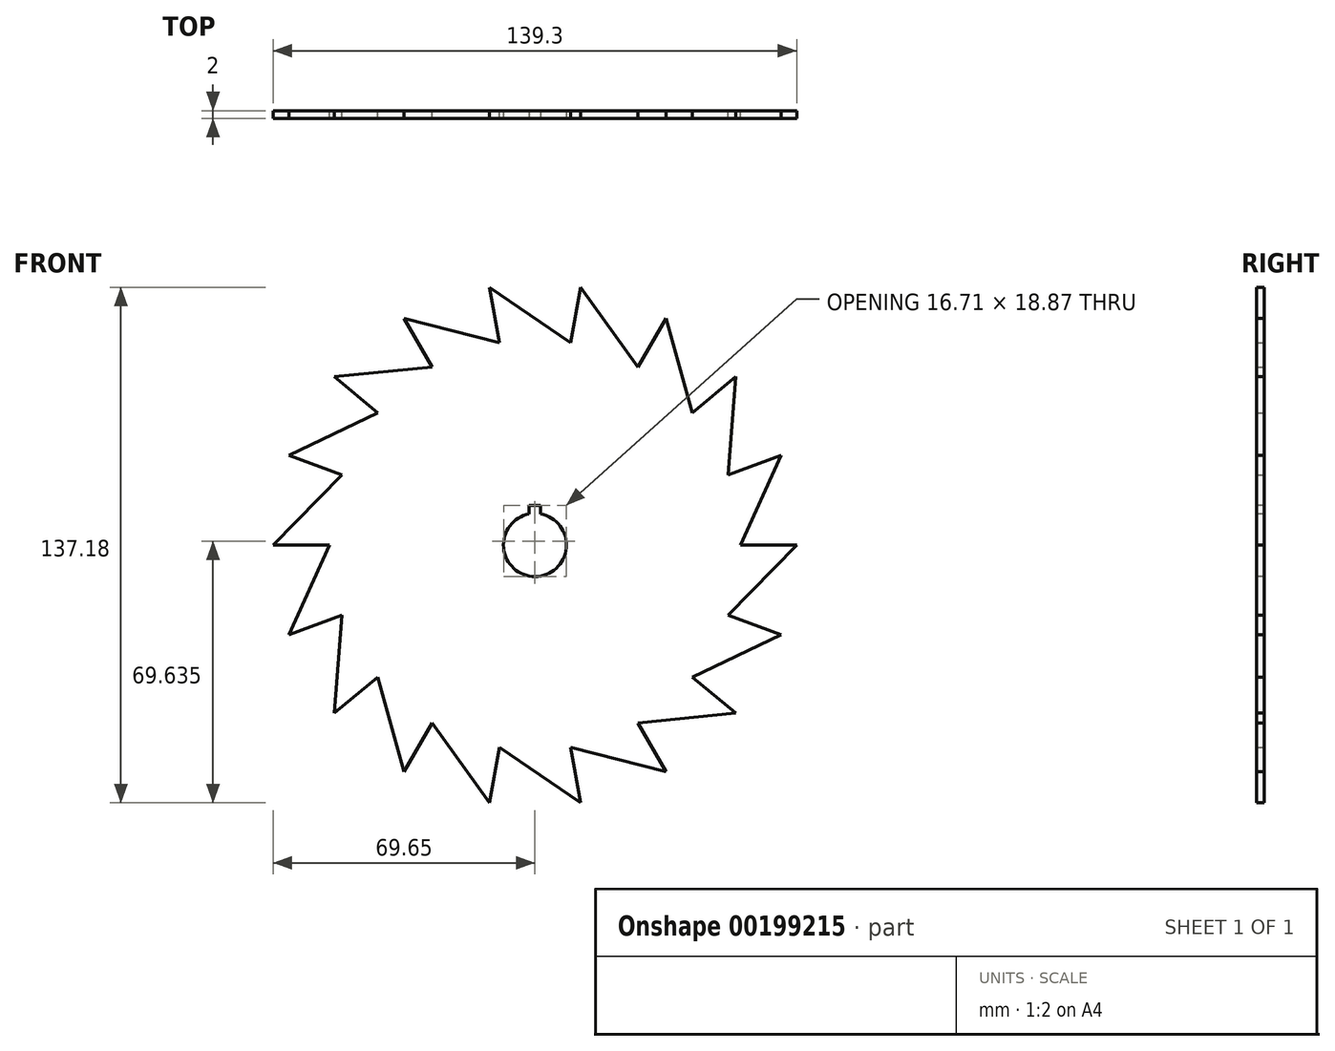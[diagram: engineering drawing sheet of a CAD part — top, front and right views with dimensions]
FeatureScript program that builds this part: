
annotation { "Feature Type Name" : "Feature", "Feature Type Description" : "" }
export const myFeature = defineFeature(function(context is Context, id is Id, definition is map)
    precondition{}
    {
        {
            var Q0;
            Q0=qCreatedBy(makeId("Front.planeOp"),FACE);
            var sketch = newSketch(context, id + "F0", { "sketchPlane" : qUnion([Q0])});
            skCircle(sketch, "E0", {"center": v(0, 0) * mm, "radius": 54.65 * mm, "construction": true});
            skCircle(sketch, "E1.0", {"center": v(0, 0) * mm, "radius": 69.65 * mm, "construction": true});
            skLineSegment(sketch, "E2", {"start": v(0, 0) * mm, "end": v(51.35, 18.7) * mm, "construction": true});
            skLineSegment(sketch, "E3", {"start": v(65.45, 23.82) * mm, "end": v(54.65, 0) * mm});
            skLineSegment(sketch, "E4", {"start": v(51.35, 18.7) * mm, "end": v(65.45, 23.82) * mm});
            skLineSegment(sketch, "E5.1.0", {"start": v(53.35, 44.77) * mm, "end": v(51.35, 18.7) * mm});
            skLineSegment(sketch, "E5.1.1", {"start": v(41.86, 35.13) * mm, "end": v(53.35, 44.77) * mm});
            skLineSegment(sketch, "E5.2.0", {"start": v(34.82, 60.32) * mm, "end": v(41.86, 35.13) * mm});
            skLineSegment(sketch, "E5.2.1", {"start": v(27.32, 47.33) * mm, "end": v(34.82, 60.32) * mm});
            skLineSegment(sketch, "E5.3.0", {"start": v(12.1, 68.6) * mm, "end": v(27.32, 47.33) * mm});
            skLineSegment(sketch, "E5.3.1", {"start": v(9.49, 53.82) * mm, "end": v(12.1, 68.6) * mm});
            skLineSegment(sketch, "E5.4.0", {"start": v(-12.1, 68.6) * mm, "end": v(9.49, 53.82) * mm});
            skLineSegment(sketch, "E5.4.1", {"start": v(-9.49, 53.82) * mm, "end": v(-12.1, 68.6) * mm});
            skLineSegment(sketch, "E5.5.0", {"start": v(-34.82, 60.32) * mm, "end": v(-9.49, 53.82) * mm});
            skLineSegment(sketch, "E5.5.1", {"start": v(-27.32, 47.33) * mm, "end": v(-34.82, 60.32) * mm});
            skLineSegment(sketch, "E5.6.0", {"start": v(-53.35, 44.77) * mm, "end": v(-27.32, 47.33) * mm});
            skLineSegment(sketch, "E5.6.1", {"start": v(-41.86, 35.13) * mm, "end": v(-53.35, 44.77) * mm});
            skLineSegment(sketch, "E5.7.0", {"start": v(-65.45, 23.82) * mm, "end": v(-41.86, 35.13) * mm});
            skLineSegment(sketch, "E5.7.1", {"start": v(-51.35, 18.7) * mm, "end": v(-65.45, 23.82) * mm});
            skLineSegment(sketch, "E5.8.0", {"start": v(-69.65, 0) * mm, "end": v(-51.35, 18.7) * mm});
            skLineSegment(sketch, "E5.8.1", {"start": v(-54.65, 0) * mm, "end": v(-69.65, 0) * mm});
            skLineSegment(sketch, "E5.9.0", {"start": v(-65.45, -23.82) * mm, "end": v(-54.65, 0) * mm});
            skLineSegment(sketch, "E5.9.1", {"start": v(-51.35, -18.7) * mm, "end": v(-65.45, -23.82) * mm});
            skLineSegment(sketch, "E5.10.0", {"start": v(-53.35, -44.77) * mm, "end": v(-51.35, -18.7) * mm});
            skLineSegment(sketch, "E5.10.1", {"start": v(-41.86, -35.13) * mm, "end": v(-53.35, -44.77) * mm});
            skLineSegment(sketch, "E5.11.0", {"start": v(-34.82, -60.32) * mm, "end": v(-41.86, -35.13) * mm});
            skLineSegment(sketch, "E5.11.1", {"start": v(-27.32, -47.33) * mm, "end": v(-34.82, -60.32) * mm});
            skLineSegment(sketch, "E5.12.0", {"start": v(-12.1, -68.6) * mm, "end": v(-27.32, -47.33) * mm});
            skLineSegment(sketch, "E5.12.1", {"start": v(-9.49, -53.82) * mm, "end": v(-12.1, -68.6) * mm});
            skLineSegment(sketch, "E5.13.0", {"start": v(12.1, -68.6) * mm, "end": v(-9.49, -53.82) * mm});
            skLineSegment(sketch, "E5.13.1", {"start": v(9.49, -53.82) * mm, "end": v(12.1, -68.6) * mm});
            skLineSegment(sketch, "E5.14.0", {"start": v(34.82, -60.32) * mm, "end": v(9.49, -53.82) * mm});
            skLineSegment(sketch, "E5.14.1", {"start": v(27.32, -47.33) * mm, "end": v(34.82, -60.32) * mm});
            skLineSegment(sketch, "E5.15.0", {"start": v(53.35, -44.77) * mm, "end": v(27.32, -47.33) * mm});
            skLineSegment(sketch, "E5.15.1", {"start": v(41.86, -35.13) * mm, "end": v(53.35, -44.77) * mm});
            skLineSegment(sketch, "E5.16.0", {"start": v(65.45, -23.82) * mm, "end": v(41.86, -35.13) * mm});
            skLineSegment(sketch, "E5.16.1", {"start": v(51.35, -18.7) * mm, "end": v(65.45, -23.82) * mm});
            skLineSegment(sketch, "E5.17.0", {"start": v(69.65, 0) * mm, "end": v(51.35, -18.7) * mm});
            skLineSegment(sketch, "E5.17.1", {"start": v(54.65, 0) * mm, "end": v(69.65, 0) * mm});
            skSolve(sketch);
        }
        {
            var Q0;
            Q0=makeQuery(id+"F0.imprint","IMPRINT",FACE,{"disambiguationData":[TD([[makeQuery(id+"F0.imprint","IMPRINT",EDGE,{"derivedFrom":sQuery(id+"F0.wireOp",EDGE,"E3")}),-1.0]])]});
            extrude(context, id + "F1", {"entities" : qUnion([Q0]), "depth" : 2 * mm});
        }
        {
            var Q0;
            Q0=makeQuery(id+"F1.opExtrude","CAP_FACE",FACE,{"disambiguationData":[OSD([sQuery(id+"F0.wireOp",EDGE,"E3"),sQuery(id+"F0.wireOp",EDGE,"E4"),sQuery(id+"F0.wireOp",EDGE,"E5.1.0"),sQuery(id+"F0.wireOp",EDGE,"E5.1.1"),sQuery(id+"F0.wireOp",EDGE,"E5.2.0"),sQuery(id+"F0.wireOp",EDGE,"E5.2.1"),sQuery(id+"F0.wireOp",EDGE,"E5.3.0"),sQuery(id+"F0.wireOp",EDGE,"E5.3.1"),sQuery(id+"F0.wireOp",EDGE,"E5.4.0"),sQuery(id+"F0.wireOp",EDGE,"E5.4.1"),sQuery(id+"F0.wireOp",EDGE,"E5.5.0"),sQuery(id+"F0.wireOp",EDGE,"E5.5.1"),sQuery(id+"F0.wireOp",EDGE,"E5.6.0"),sQuery(id+"F0.wireOp",EDGE,"E5.6.1"),sQuery(id+"F0.wireOp",EDGE,"E5.7.0"),sQuery(id+"F0.wireOp",EDGE,"E5.7.1"),sQuery(id+"F0.wireOp",EDGE,"E5.8.0"),sQuery(id+"F0.wireOp",EDGE,"E5.8.1"),sQuery(id+"F0.wireOp",EDGE,"E5.9.0"),sQuery(id+"F0.wireOp",EDGE,"E5.9.1"),sQuery(id+"F0.wireOp",EDGE,"E5.10.0"),sQuery(id+"F0.wireOp",EDGE,"E5.10.1"),sQuery(id+"F0.wireOp",EDGE,"E5.11.0"),sQuery(id+"F0.wireOp",EDGE,"E5.11.1"),sQuery(id+"F0.wireOp",EDGE,"E5.12.0"),sQuery(id+"F0.wireOp",EDGE,"E5.12.1"),sQuery(id+"F0.wireOp",EDGE,"E5.13.0"),sQuery(id+"F0.wireOp",EDGE,"E5.13.1"),sQuery(id+"F0.wireOp",EDGE,"E5.14.0"),sQuery(id+"F0.wireOp",EDGE,"E5.14.1"),sQuery(id+"F0.wireOp",EDGE,"E5.15.0"),sQuery(id+"F0.wireOp",EDGE,"E5.15.1"),sQuery(id+"F0.wireOp",EDGE,"E5.16.0"),sQuery(id+"F0.wireOp",EDGE,"E5.16.1"),sQuery(id+"F0.wireOp",EDGE,"E5.17.0"),sQuery(id+"F0.wireOp",EDGE,"E5.17.1")])],"isStart":false});
            var sketch = newSketch(context, id + "F2", { "sketchPlane" : qUnion([Q0])});
            skArc(sketch, "E6", {"start": v(-1.51, 8.25) * mm, "mid": v(0, -8.39) * mm, "end": v(1.51, 8.25) * mm});
            skLineSegment(sketch, "E7.bottom", {"start": v(-1.51, 10.48) * mm, "end": v(1.51, 10.48) * mm});
            skLineSegment(sketch, "E7.left", {"start": v(-1.51, 10.48) * mm, "end": v(-1.51, 8.25) * mm});
            skLineSegment(sketch, "E7.right", {"start": v(1.51, 10.48) * mm, "end": v(1.51, 8.25) * mm});
            skSolve(sketch);
        }
        {
            var Q0;
            Q0=makeQuery(id+"F2.imprint","IMPRINT",FACE,{"disambiguationData":[TD([[makeQuery(id+"F2.imprint","IMPRINT",EDGE,{"derivedFrom":sQuery(id+"F2.wireOp",EDGE,"E6")}),1.0]])]});
            extrude(context, id + "F3", {"entities" : qUnion([Q0]), "operationType" : NewBodyOperationType.REMOVE, "oppositeDirection" : true, "depth" : 25 * mm});
        }
    });
